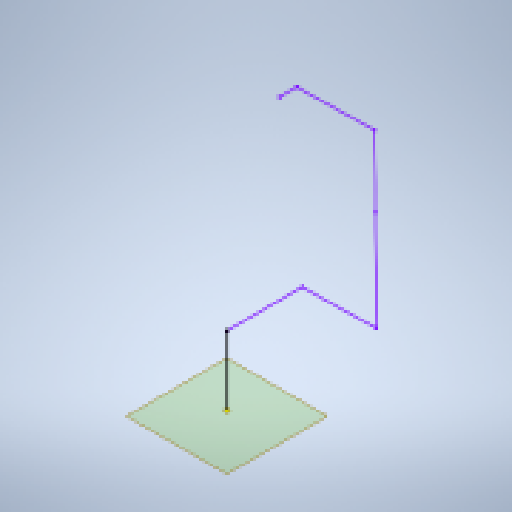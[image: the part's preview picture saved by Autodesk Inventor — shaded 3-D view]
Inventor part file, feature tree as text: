
AUTODESK INVENTOR PART (.ipt)
format: ipt  version: 2025 (Build 290162000, 162)  size: 165,888 bytes
history: native  units: in
note: dims shown in document units (in); Inventor stores cm internally (conversion verified against a paired STEP export)
features: other x1, plane x1, sketch x1
ambient origin geometry x8: Origin, YZ Plane, XZ Plane, XY Plane, X Axis, Y Axis, Z Axis, Center Point
feature tree (3):
  other  "Work Point1"
  plane  "Work Plane1"
  sketch  "3D Sketch1"
